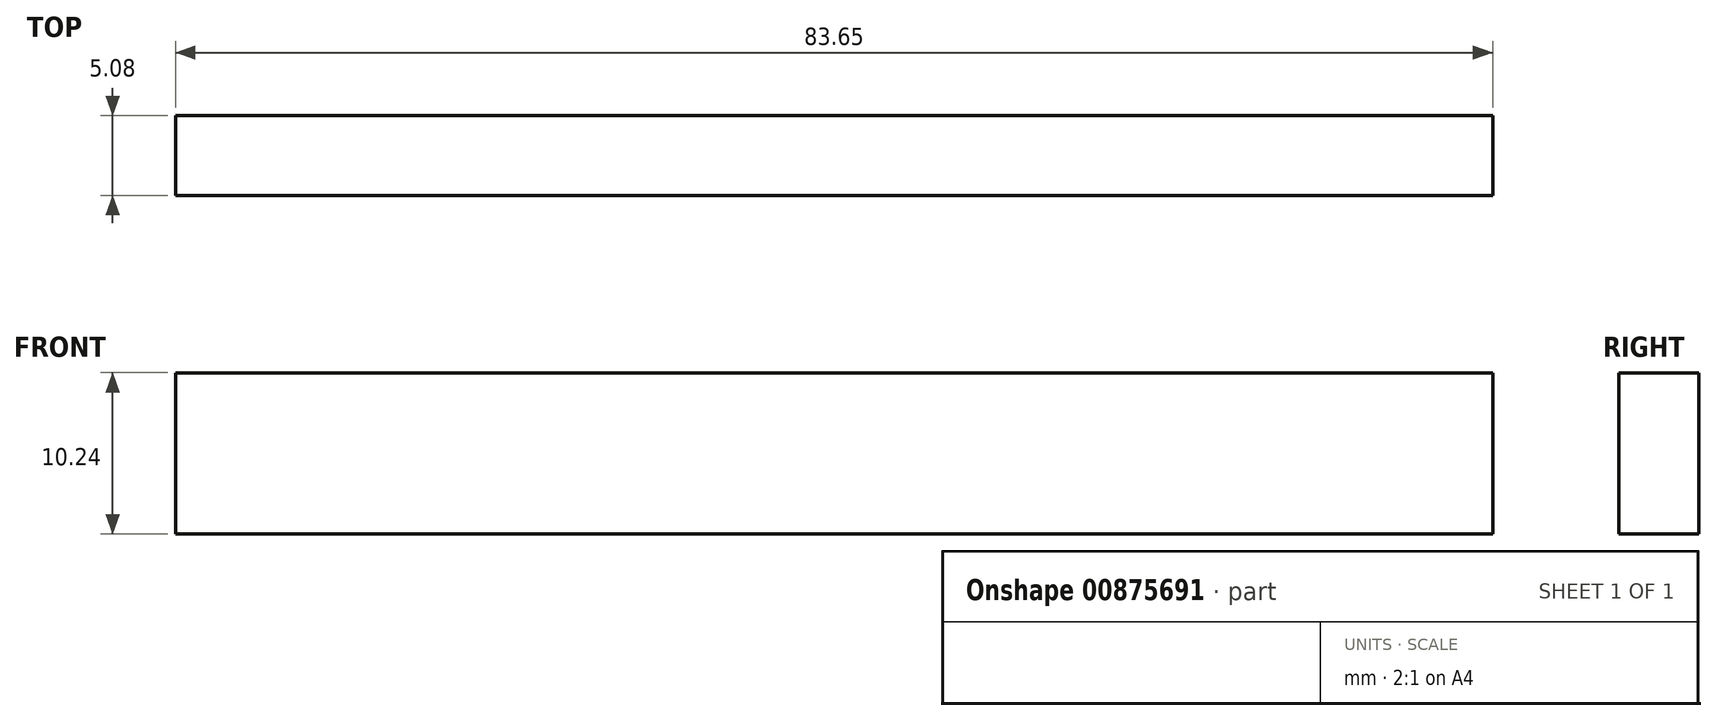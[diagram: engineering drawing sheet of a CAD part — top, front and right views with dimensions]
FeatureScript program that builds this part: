
annotation { "Feature Type Name" : "Feature", "Feature Type Description" : "" }
export const myFeature = defineFeature(function(context is Context, id is Id, definition is map)
    precondition{}
    {
        {
            var Q0;
            Q0=qCreatedBy(makeId("Front.planeOp"),FACE);
            var sketch = newSketch(context, id + "F0", { "sketchPlane" : qUnion([Q0])});
            skLineSegment(sketch, "E0.bottom", {"start": v(-37.04, 8.57) * mm, "end": v(46.61, 8.57) * mm});
            skLineSegment(sketch, "E0.top", {"start": v(-37.04, 18.8) * mm, "end": v(46.61, 18.8) * mm});
            skLineSegment(sketch, "E0.left", {"start": v(-37.04, 8.57) * mm, "end": v(-37.04, 18.8) * mm});
            skLineSegment(sketch, "E0.right", {"start": v(46.61, 8.57) * mm, "end": v(46.61, 18.8) * mm});
            skSolve(sketch);
        }
        {
            var Q0;
            Q0 = qSketchRegion(id + "F0", true);
            extrude(context, id + "F1", {"entities" : qUnion([Q0]), "depth" : 5.08 * mm, "offsetDistance" : 25.4 * mm});
        }
    });
